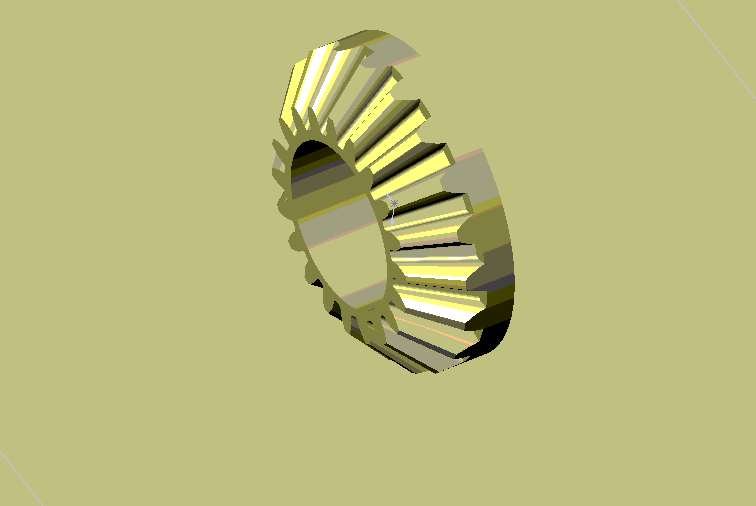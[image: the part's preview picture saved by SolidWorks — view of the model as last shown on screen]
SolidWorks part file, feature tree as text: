
SOLIDWORKS PART (.sldprt)
format: sldprt  version: not decoded by parser v0  size: 641,536 bytes
history: native  units: mm
features: sketch x22, plane x4, cut_extrude x3, material x1, fillet x1, pattern_circular x1, extrude x1 + 1 further entry (+9 scaffold rows collapsed)
feature tree (43):
  scaffold x9  (default folders/planes/origin — collapsed)
  material  "Matériau <non spécifié>"
  plane  "Plane1"
  plane  "Plane2"
  plane  "Plane3"
  "Famille de pièces"
  sketch  "Esquisse1"  dims[c1.D2=11.0mm c1.D1=42.0mm c2.D1=9.0deg]
  sketch  "Esquisse2"  dims[c1.D2=~10.778873mm c1.D1=37.0mm c2.D1=~9.769674deg]
  sketch  "Esquisse3"  dims[c1.D2=~10.557746mm c1.D1=33.0mm c2.D1=~10.373081deg]
  sketch  "Esquisse4"  dims[c1.D2=~10.336619mm c1.D1=30.0mm c2.D1=~10.707917deg]
  sketch  "Esquisse5"  dims[c1.D2=~11.366667mm c1.D1=46.0mm c2.D1=7.4521deg]
  sketch  "Esquisse6"  dims[c1.D2=~11.733333mm c1.D1=50.0mm c2.D1=~5.640619deg]
  sketch  "Esquisse7"  dims[c1.D2=12.1mm c1.D1=54.0mm c2.D1=~3.619426deg]
  plane  "Plan1"  Offset=4mm
  sketch  "Esquisse8"  dims[c1.D2=7.0mm c1.D1=18.0mm c2.D1=9.0deg]
  sketch  "Esquisse9"  dims[c1.D2=~6.859283mm c1.D1=15.0mm c2.D1=~9.769674deg]
  sketch  "Esquisse10"  dims[c1.D2=~6.718566mm c1.D1=13.0mm c2.D1=~10.373081deg]
  sketch  "Esquisse11"  dims[c1.D2=~6.577848mm c1.D1=12.0mm c2.D1=~10.707917deg]
  sketch  "Esquisse12"  dims[c1.D2=~7.233333mm c1.D1=20.0mm c2.D1=7.4521deg]
  sketch  "Esquisse13"  dims[c1.D2=~7.466667mm c1.D1=21.0mm c2.D1=~5.640619deg]
  sketch  "Esquisse14"  dims[c1.D2=7.7mm c1.D1=22.0mm c2.D1=~3.619426deg]
  sketch  "Esquisse15"  dims[c1.D2=9.625mm c1.D1=23.0mm c2.D1=~10.707917deg]
  sketch  "Esquisse16"  dims[c1.D2=6.125mm c1.D1=10.0mm c2.D1=~10.707917deg]
  sketch  "Esquisse17"  dims[D1=19.25mm]
  sketch  "Esquisse18"  dims[D1=12.25mm]
  fillet  "Congé1"  Radius=0.25mm
  pattern_circular  "Répétition circulaire1"  Count=20 Angle=360deg
  sketch  "Esquisse19"  dims[D1=21.0mm]
  extrude  "Boss.-Extru.1"  Depth=2mm
  sketch  "Esquisse20"  dims[D1=10.0mm]
  sketch  "Esquisse21"  dims[D1=11.0mm]
  cut_extrude  "Enlèv. mat.-Extru.1"  [1 undecoded]
  cut_extrude  "Enlèv. mat.-Extru.2"  [1 undecoded]
  sketch  "Esquisse22"
  cut_extrude  "Enlèv. mat.-Extru.3"  [1 undecoded]
decode coverage: 24 of 28 modeling features carry decoded parameters; 1 rows unclassified (native names shown)
note: ~ marks probable driven/reference dimensions
note: 3 parameter values undecoded
summary: no parameter record found for 3 features
note: suppression state not decoded; provenance and decode notes live in map.json
